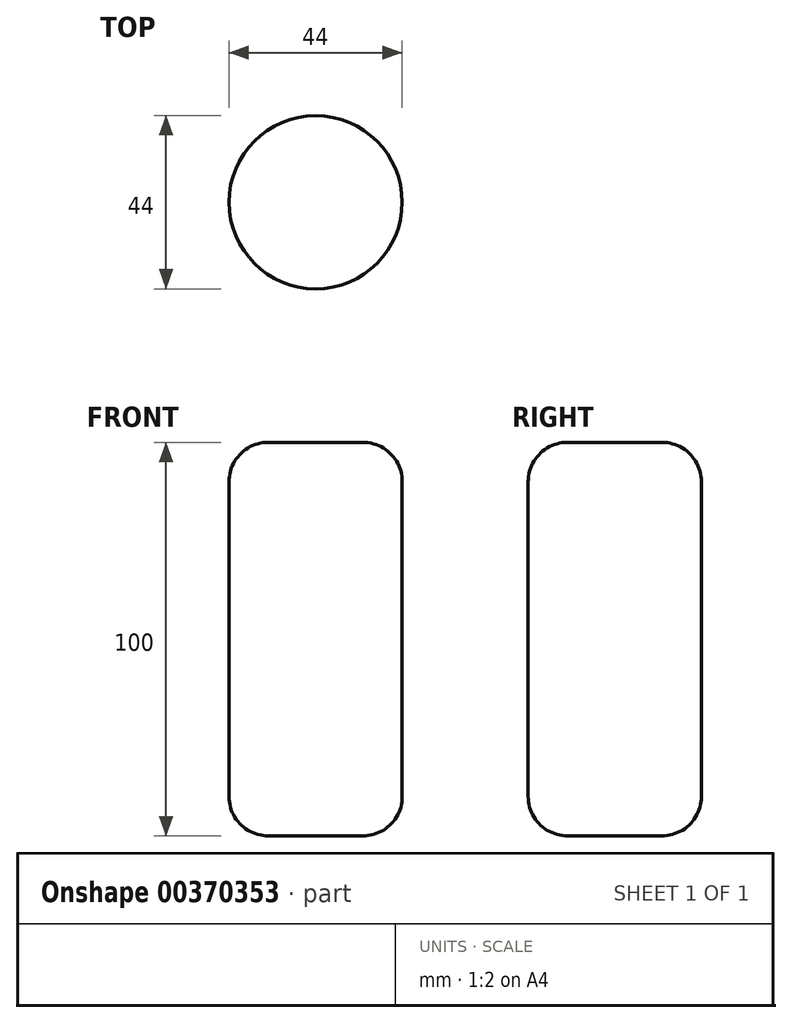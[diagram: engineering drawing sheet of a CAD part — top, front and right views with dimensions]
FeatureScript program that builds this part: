
annotation { "Feature Type Name" : "Feature", "Feature Type Description" : "" }
export const myFeature = defineFeature(function(context is Context, id is Id, definition is map)
    precondition{}
    {
        {
            var Q0;
            Q0=qCreatedBy(makeId("Top.planeOp"),FACE);
            var sketch = newSketch(context, id + "F0", { "sketchPlane" : qUnion([Q0])});
            skCircle(sketch, "E0", {"center": v(0, 0) * mm, "radius": 22 * mm});
            skSolve(sketch);
        }
        {
            var Q0;
            Q0=makeQuery(id+"F0.imprint","IMPRINT",FACE,{"disambiguationData":[TD([[makeQuery(id+"F0.imprint","IMPRINT",EDGE,{"derivedFrom":sQuery(id+"F0.wireOp",EDGE,"E0")}),1.0]])]});
            extrude(context, id + "F1", {"entities" : qUnion([Q0]), "depth" : 100 * mm});
        }
        {
            var Q0;
            Q0=makeQuery(id+"F1.opExtrude","CAP_FACE",FACE,{"disambiguationData":[OSD([sQuery(id+"F0.wireOp",EDGE,"E0")])],"isStart":false});
            var Q1;
            Q1=makeQuery(id+"F1.opExtrude","CAP_EDGE",EDGE,{"disambiguationData":[OSD([sQuery(id+"F0.wireOp",EDGE,"E0")])],"isStart":true});
            fillet(context, id + "F2", {"entities" : qUnion([Q0, Q1]), "radius" : 10 * mm, "tangentPropagation" : true, "allowEdgeOverflow" : false});
        }
    });
